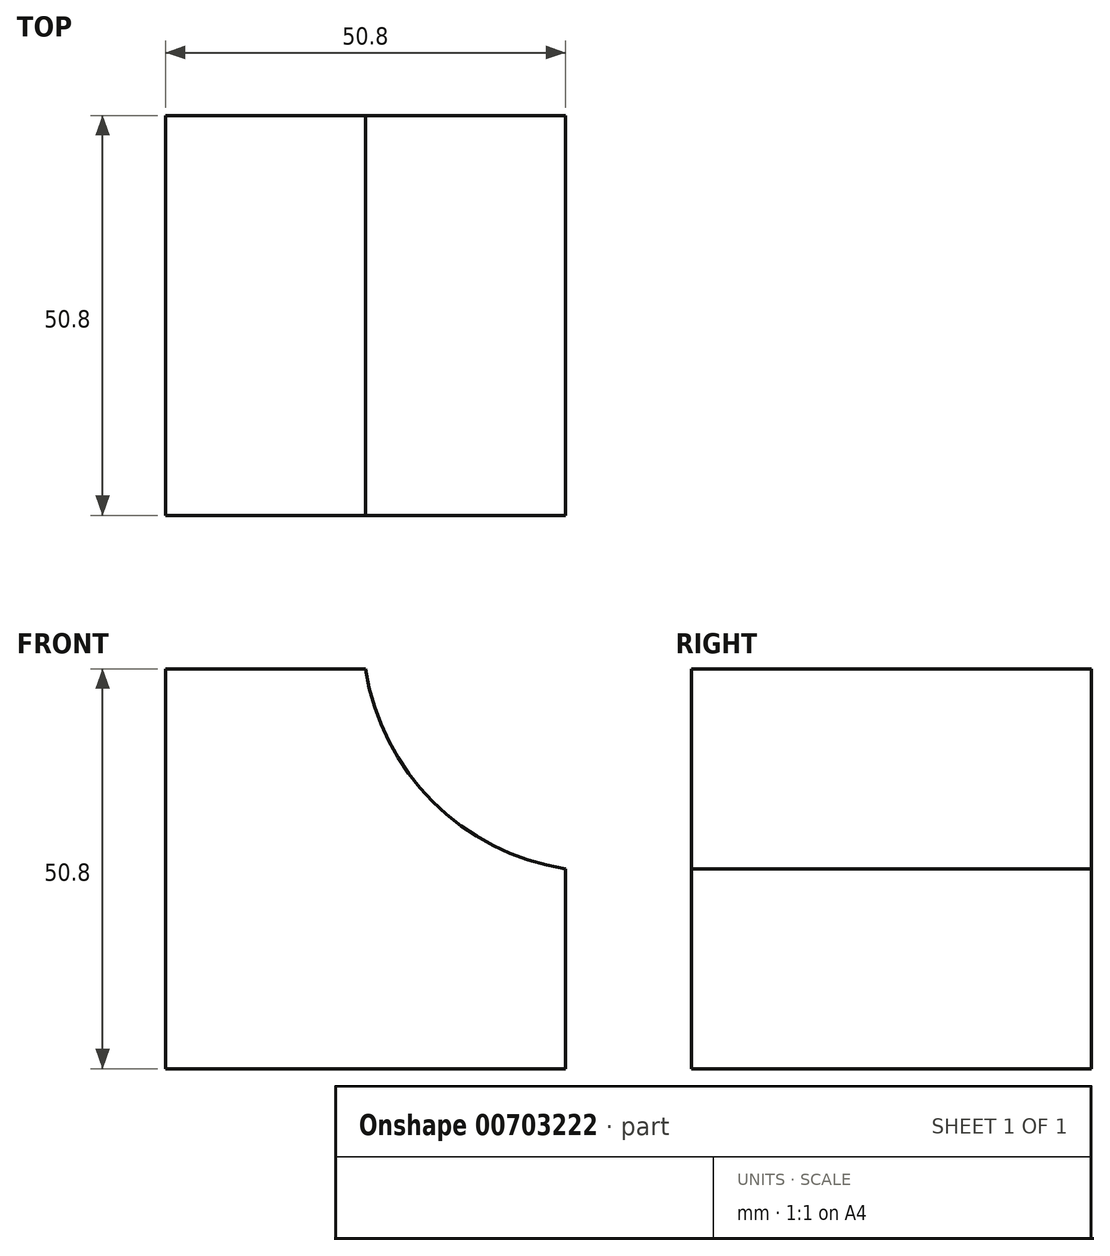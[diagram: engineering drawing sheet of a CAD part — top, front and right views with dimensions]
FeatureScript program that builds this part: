
annotation { "Feature Type Name" : "Feature", "Feature Type Description" : "" }
export const myFeature = defineFeature(function(context is Context, id is Id, definition is map)
    precondition{}
    {
        {
            var Q0;
            Q0=qCreatedBy(makeId("Front.planeOp"),FACE);
            var sketch = newSketch(context, id + "F0", { "sketchPlane" : qUnion([Q0])});
            skLineSegment(sketch, "E0", {"start": v(18.43, 11.17) * mm, "end": v(18.43, -14.23) * mm});
            skLineSegment(sketch, "E1", {"start": v(18.43, -14.23) * mm, "end": v(-32.37, -14.23) * mm});
            skLineSegment(sketch, "E2", {"start": v(-32.37, -14.23) * mm, "end": v(-32.37, 36.57) * mm});
            skLineSegment(sketch, "E3", {"start": v(-32.37, 36.57) * mm, "end": v(-6.97, 36.57) * mm});
            skArc(sketch, "E4", {"start": v(-6.97, 36.57) * mm, "mid": v(1.56, 19.7) * mm, "end": v(18.43, 11.17) * mm});
            skSolve(sketch);
        }
        {
            var Q0;
            Q0 = qSketchRegion(id + "F0", true);
            extrude(context, id + "F1", {"entities" : qUnion([Q0]), "depth" : 50.8 * mm, "offsetDistance" : 25.4 * mm});
        }
    });
